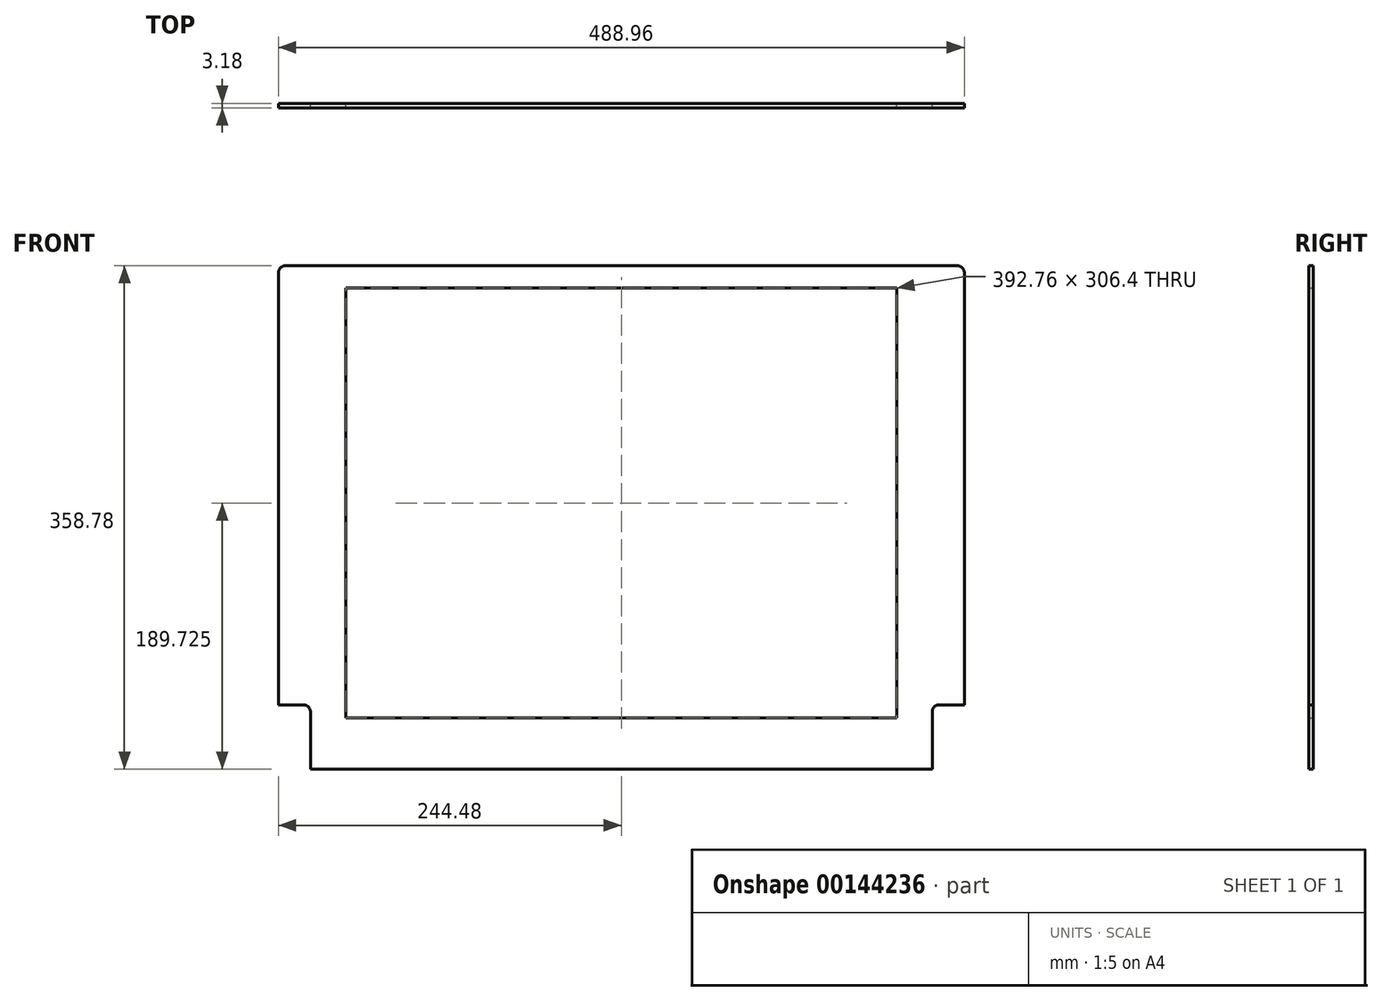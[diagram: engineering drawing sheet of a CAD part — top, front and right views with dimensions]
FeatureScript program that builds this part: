
annotation { "Feature Type Name" : "Feature", "Feature Type Description" : "" }
export const myFeature = defineFeature(function(context is Context, id is Id, definition is map)
    precondition{}
    {
        {
            var Q0;
            Q0=qCreatedBy(makeId("Right.planeOp"),FACE);
            var sketch = newSketch(context, id + "F0", { "sketchPlane" : qUnion([Q0])});
            skLineSegment(sketch, "E0", {"start": v(0, 0) * mm, "end": v(0, 358.77) * mm});
            skLineSegment(sketch, "E1", {"start": v(-25.4, 0) * mm, "end": v(0, 0) * mm, "construction": true});
            skLineSegment(sketch, "E2.0", {"start": v(3.18, 0) * mm, "end": v(3.18, 358.78) * mm});
            skLineSegment(sketch, "E3", {"start": v(0, 358.78) * mm, "end": v(3.18, 358.78) * mm});
            skLineSegment(sketch, "E4", {"start": v(0, 0) * mm, "end": v(3.18, 0) * mm});
            skSolve(sketch);
        }
        {
            var Q0;
            Q0 = qSketchRegion(id + "F0", true);
            extrude(context, id + "F1", {"entities" : qUnion([Q0]), "flatOperationType" : FlatOperationType.REMOVE, "endBound" : BoundingType.SYMMETRIC, "offsetDistance" : 25.4 * mm, "depth" : 488.95 * mm, "domain" : OperationDomain.MODEL});
        }
        {
            var Q0;
            Q0=makeQuery(id+"F1.opExtrude","SWEPT_FACE",FACE,{"disambiguationData":[OSD([sQuery(id+"F0.wireOp",EDGE,"E2.0")])]});
            var sketch = newSketch(context, id + "F2", { "sketchPlane" : qUnion([Q0])});
            skLineSegment(sketch, "E5.bottom", {"start": v(244.48, 45.85) * mm, "end": v(221.62, 45.85) * mm});
            skLineSegment(sketch, "E5.top", {"start": v(244.48, -30.35) * mm, "end": v(221.62, -30.35) * mm});
            skLineSegment(sketch, "E5.left", {"start": v(244.47, 45.85) * mm, "end": v(244.48, -30.35) * mm});
            skLineSegment(sketch, "E5.right", {"start": v(221.62, 45.85) * mm, "end": v(221.62, -30.35) * mm});
            skLineSegment(sketch, "E6.bottom", {"start": v(-244.48, 45.85) * mm, "end": v(-221.62, 45.85) * mm});
            skLineSegment(sketch, "E6.top", {"start": v(-244.48, -30.35) * mm, "end": v(-221.62, -30.35) * mm});
            skLineSegment(sketch, "E6.left", {"start": v(-244.48, 45.85) * mm, "end": v(-244.48, -30.35) * mm});
            skLineSegment(sketch, "E6.right", {"start": v(-221.62, 45.85) * mm, "end": v(-221.62, -30.35) * mm});
            skSolve(sketch);
        }
        {
            var Q0;
            Q0 = qSketchRegion(id + "F2", true);
            extrude(context, id + "F3", {"entities" : qUnion([Q0]), "operationType" : NewBodyOperationType.REMOVE, "oppositeDirection" : true, "depth" : 25.4 * mm});
        }
        {
            var Q0;
            Q0=makeQuery(id+"F1.opExtrude","SWEPT_FACE",FACE,{"disambiguationData":[OSD([sQuery(id+"F0.wireOp",EDGE,"E2.0")])]});
            var sketch = newSketch(context, id + "F4", { "sketchPlane" : qUnion([Q0])});
            skLineSegment(sketch, "E7.bottom", {"start": v(-196.38, 342.93) * mm, "end": v(196.38, 342.93) * mm});
            skLineSegment(sketch, "E7.top", {"start": v(-196.38, 36.53) * mm, "end": v(196.38, 36.53) * mm});
            skLineSegment(sketch, "E7.left", {"start": v(-196.38, 342.93) * mm, "end": v(-196.38, 36.53) * mm});
            skLineSegment(sketch, "E7.right", {"start": v(196.38, 342.93) * mm, "end": v(196.38, 36.53) * mm});
            skPoint(sketch, "E8", {"position": v(0, 342.93) * mm});
            skPoint(sketch, "E9", {"position": v(0, 358.78) * mm});
            skSolve(sketch);
        }
        {
            var Q0;
            Q0 = qSketchRegion(id + "F4", true);
            extrude(context, id + "F5", {"entities" : qUnion([Q0]), "operationType" : NewBodyOperationType.REMOVE, "oppositeDirection" : true, "depth" : 25.4 * mm});
        }
        {
            var Q0;
            Q0=makeQuery(id+"F1.opExtrude","CAP_EDGE",EDGE,{"disambiguationData":[OSD([sQuery(id+"F0.wireOp",EDGE,"E3")])],"isStart":false});
            var Q1;
            Q1=makeQuery(id+"F3.boolean.opBoolean","COPY",EDGE,{"derivedFrom":makeQuery(id+"F3.opExtrude","SWEPT_EDGE",EDGE,{"disambiguationData":[OSD([sQuery(id+"F0.wireOp",EDGE,"E2.0"),sQuery(id+"F2.wireOp",EDGE,"E6.bottom"),sQuery(id+"F2.wireOp",EDGE,"E6.left")])]})});
            var Q2;
            Q2=makeQuery(id+"F3.boolean.opBoolean","COPY",EDGE,{"derivedFrom":makeQuery(id+"F3.opExtrude","SWEPT_EDGE",EDGE,{"disambiguationData":[OSD([sQuery(id+"F2.wireOp",EDGE,"E6.bottom"),sQuery(id+"F2.wireOp",EDGE,"E6.right")])]})});
            var Q3;
            Q3=makeQuery(id+"F3.boolean.opBoolean","COPY",EDGE,{"derivedFrom":makeQuery(id+"F3.opExtrude","SWEPT_EDGE",EDGE,{"disambiguationData":[OSD([sQuery(id+"F0.wireOp",EDGE,"E2.0"),sQuery(id+"F2.wireOp",EDGE,"E5.bottom"),sQuery(id+"F2.wireOp",EDGE,"E5.left")])]})});
            var Q4;
            Q4=makeQuery(id+"F3.boolean.opBoolean","COPY",EDGE,{"derivedFrom":makeQuery(id+"F3.opExtrude","SWEPT_EDGE",EDGE,{"disambiguationData":[OSD([sQuery(id+"F2.wireOp",EDGE,"E5.bottom"),sQuery(id+"F2.wireOp",EDGE,"E5.right")])]})});
            var Q5;
            Q5=makeQuery(id+"F1.opExtrude","CAP_EDGE",EDGE,{"disambiguationData":[OSD([sQuery(id+"F0.wireOp",EDGE,"E3")])],"isStart":true});
            fillet(context, id + "F6", {"entities" : qUnion([Q0, Q1, Q2, Q3, Q4, Q5]), "radius" : 5.08 * mm, "tangentPropagation" : true, "allowEdgeOverflow" : false});
        }
    });
